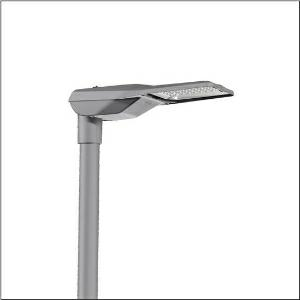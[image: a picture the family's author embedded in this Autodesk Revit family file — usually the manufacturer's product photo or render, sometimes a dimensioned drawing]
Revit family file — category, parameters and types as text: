
# Revit family: streetlight_sl_21_mini___p0_8ab_5xe2r33s08hb_da28
name_source: partatom
category: Lighting Fixtures
units: mm (PartAtom-declared; Revit-internal decimal feet)

## family parameters
Cut with Voids When Loaded = No
Host = Face
Light Source = No
Part Type = Normal
Room Calculation Point = No
Round Connector Dimension = Use Diameter
Shared = No

## types (1)
- --- (1 x LED, 7850 lm, 66 W, 3000K)
    Apparent Load = 66 VA
    CIE Flux Codes = 36 71 98 100 100
    Color Rendering = 70
    Color Temperature = 3000K
    Default Elevation = 1800 mm
    Description = Streetlight SL 21 mini, mast luminaire, primary light control with lens, of PMMA, primary optical cover: cover, of toughened safety glass, transparent, light distribution: P0.8aB, light emission: direct distribution, primary light characteristic: asymmetric, installation type: post-top, side-entry, LED, High Power LED, rated luminous flux: 7.850lm, luminous efficacy: 119lm/W, light colour: 730, colour temperature: 3000K, control gear: D4i, control: pre-setting: logarithmic dimming characteristic, flexible luminous flux parameterisation, time-dependent luminous flux control, constant luminous flux control, overheat protection, mains connection: 220..240V, AC, 50/60Hz, start of lifetime: 66W, end of service life: 69W, reduction: 30W, luminaire housing, of diecast aluminium, powder-coated, SITECO metallic grey (DB 702S), corrosivity category C5 high according to DIN EN ISO 12944, multi-level sealing system, sealing non-destructively replaceable, inclination adjustable: 0°, 5°, 10°, 15°, please order mast flange separately, length: 628mm, width: 235mm, height: 110mm, mast flange for spigot size: 42mm (side-entry): 5XC10008XM4, 60/48mm (side-entry/post-top): 5XC10108XM2, 76/60mm (side-entry/post-top): 5XC10108XM1, mounting height: 4..8m, Smart Interface above, protection rating (complete): IP66, insulation class (complete): insulation class II (safety insulation), certification: CE, ENEC, ENEC+, VDE, impact resistance: IK10, permissible operating ambient temperature for outdoor applications: -40..+50°C, standard-compliant lighting for roads and squares, packaging unit: 1 piece

Light Distribution: P0.8aB
    Height = 110 mm
    Lamp = 1 x LED
    Lamp Light Flux = 7850 lm
    Lamp Power = 66 W
    Lamp count = 1
    Length = 625 mm
    Luminous efficacy = 119 lm/W
    Manufacturer = Siteco
    ModVariant = No
    Model = 5XE2R33S08HB
    Number of Poles = 1
    OnlyDefault = Yes
    Power Factor = 1
    Product Name = Streetlight SL 21 mini | P0.8aB
    Product group = mast luminaire | pylon top
    ProductGroupID = 6100
    Protection Class = Protection class II
    Protection Degree = IP 66
    RLX_Detail_Level = 1
    RLX_Emergency_Light_Flux = 0 lm
    RLX_Emergency_Type = 0
    RLX_Emergency_Type_DB = No
    RlxData = <blob elided: 91709 chars, md5=08821cab>
    Socket = socket
    Standby Power = 0 W
    System Light Flux = 7850 lm
    System Power = 66 W
    Type Comments = factory setting: luminous flux: 100 % | dim-lin: 254 | 670 mA
    Type Image = l_1003515.jpg
    URL = http://relux.com
    VarID = @adj_082637
    Voltage = 0 V
    Weight = 0.00 kg
    Width = 234 mm

## geometry (parser evidence)
native form markers: Blend x4, Sweep x10
no freeform markers — native parametric forms only
